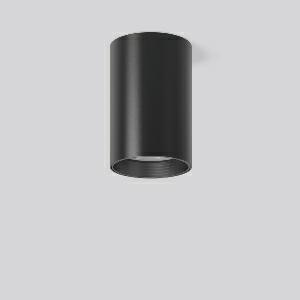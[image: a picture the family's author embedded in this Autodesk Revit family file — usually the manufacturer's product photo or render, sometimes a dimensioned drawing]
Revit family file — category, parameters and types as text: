
# Revit family: heledon_maxi_a_931229_003_3_76_746d
name_source: partatom
category: Lighting Fixtures
units: mm (PartAtom-declared; Revit-internal decimal feet)

## family parameters
Cut with Voids When Loaded = No
Host = Face
Light Source = No
Part Type = Normal
Room Calculation Point = No
Round Connector Dimension = Use Diameter
Shared = No

## types (1)
- HELEDON maxi A (1 x LED Modul 935, 3650 lm, 3500)
    Apparent Load = 35 VA
    Approval mark = CE
    CIE Flux Codes = 96 100 100 100 100
    Color Rendering = 92
    Color Temperature = 3500
    Default Elevation = 1800 mm
    Description = Series: HELEDON maxi
Cylindrical surface-mounted downlight. Housing: die-cast aluminium, powder-coated. Internal ceiling frame polycarbonate with bayonet mounting. Black plastic ring and recessed LED to prevent glare from the side. Optical assembly with lens made of plastic (polycarbonate) for the best homogeneous light distribution - can be changed without tools. Best colour rendering index Ra>90. Suitable for Ceiling mounting. Easy installation with a separate ceiling frame with bayonet mounting and plug connection. Driver integrated. Connected via plug-in connector. High quality converter without flickering and stroboscopic effect. The following accessories can be mounted without use of tools: interchangeable lenses, decorative glasses, honeycomb louvre, clear and frosted diffusers, white interchangeable plastic ring. 
Colour: deep black, matt (RAL 9005)
Diameter: 123 mm
Height: 183 mm
Lamp: LED
Socket: without socket
Colour temperature: 3500K
Colour rendering index (CRI): 92
System power: 35 W
Rated luminous flux: 3650 lm
Luminous efficiency: 104 lm/W
Control gear: Converter, dimmable, DALI
Protection class: I
Type of protection: IP 20
    Height = 183 mm
    Lamp = 1 x LED Modul 935
    Lamp Light Flux = 3650 lm
    Lamp count = 1
    Length = 123 mm
    Lifetime = 50000 h
    Luminous efficacy = 104 lm/W
    Manufacturer = RZB
    ModVariant = No
    Model = 931229.003.3.76
    Mounting Place = Ceiling
    Mounting Type = Surface mounted
    Number of Poles = 1
    OnlyDefault = Yes
    Power Factor = 1
    Product Name = HELEDON maxi A
    Product group = Surface mounted downlights
    ProductGroupID = 302
    Protection Class = Protection class I
    Protection Degree = IP 20
    RLX_Detail_Level = 1
    RLX_Emergency_Light_Flux = 0 lm
    RLX_Emergency_Type = 0
    RLX_Emergency_Type_DB = No
    RlxData = <blob elided: 97217 chars, md5=1747e185>
    Socket = socket
    Standby Power = 0 W
    System Light Flux = 3650 lm
    System Power = 35 W
    Type Comments = Product without accessories
    Type Image = 931193.003.jpg
    URL = http://relux.com
    VarID = ---
    Voltage = 230 V
    Voltage Range = 220-240 V
    Weight = 0.00 kg
    Width = 0 mm  [stored 0 ft]

note: [stored X ft] marks values corroborated as IEEE doubles in the binary element streams (Revit-internal decimal feet)

## geometry (parser evidence)
native form markers: Blend x4, Sweep x11
no freeform markers — native parametric forms only
